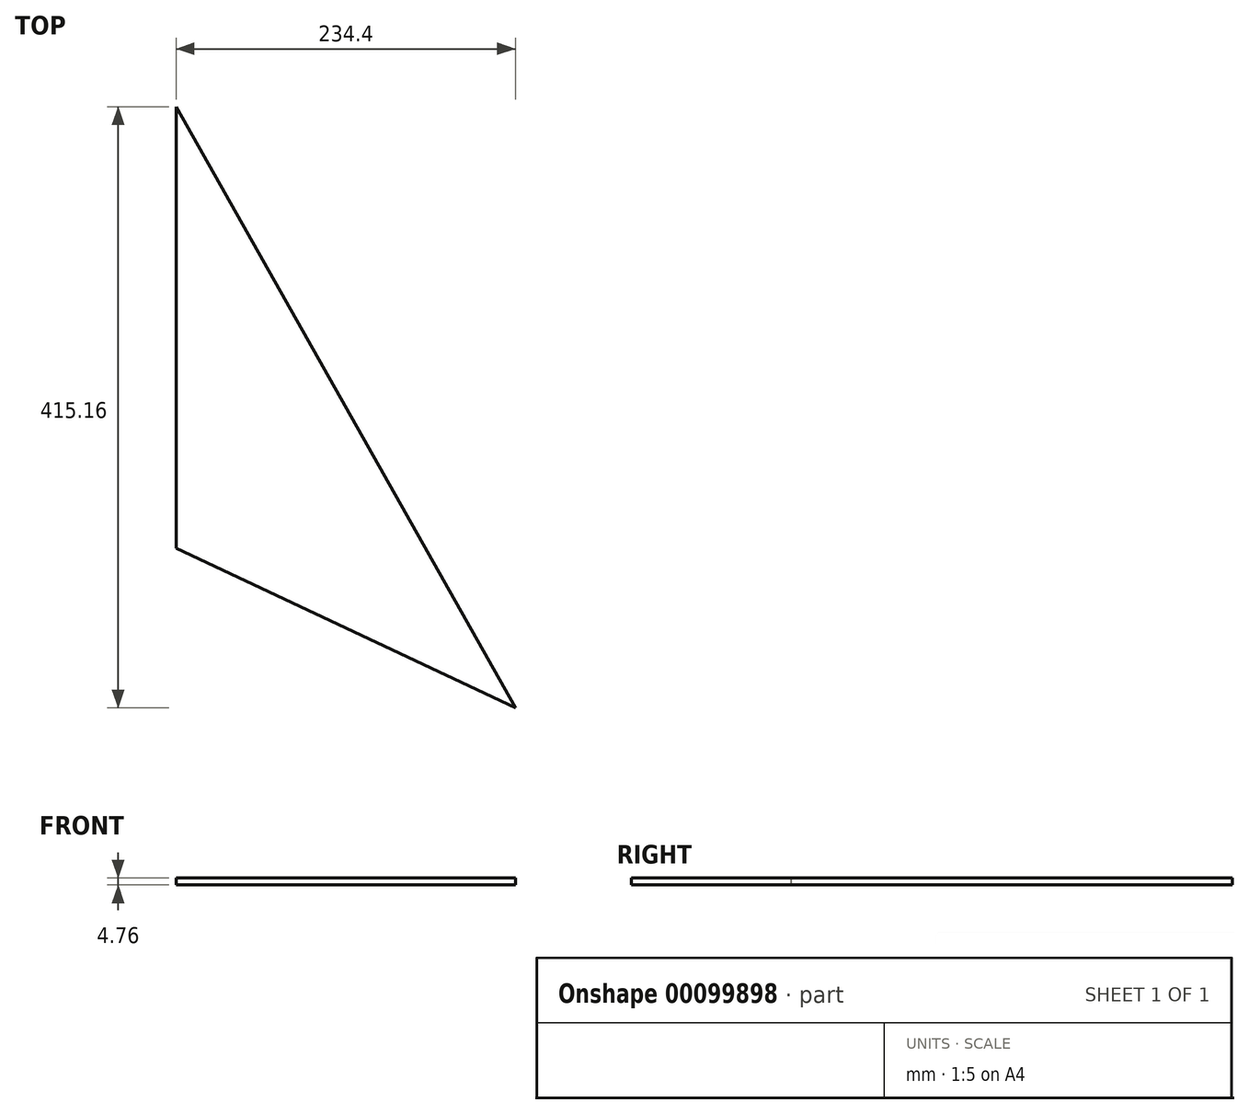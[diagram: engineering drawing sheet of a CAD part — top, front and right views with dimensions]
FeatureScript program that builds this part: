
annotation { "Feature Type Name" : "Feature", "Feature Type Description" : "" }
export const myFeature = defineFeature(function(context is Context, id is Id, definition is map)
    precondition{}
    {
        {
            var Q0;
            Q0=qCreatedBy(makeId("Top.planeOp"),FACE);
            var sketch = newSketch(context, id + "F0", { "sketchPlane" : qUnion([Q0])});
            skLineSegment(sketch, "E0", {"start": v(0, 0) * mm, "end": v(0, 304.8) * mm});
            skLineSegment(sketch, "E1", {"start": v(0, 304.8) * mm, "end": v(234.4, -110.36) * mm});
            skLineSegment(sketch, "E2", {"start": v(234.4, -110.36) * mm, "end": v(0, 0) * mm});
            skSolve(sketch);
        }
        {
            var Q0;
            Q0 = qSketchRegion(id + "F0", true);
            extrude(context, id + "F1", {"entities" : qUnion([Q0]), "depth" : 4.76 * mm});
        }
    });
